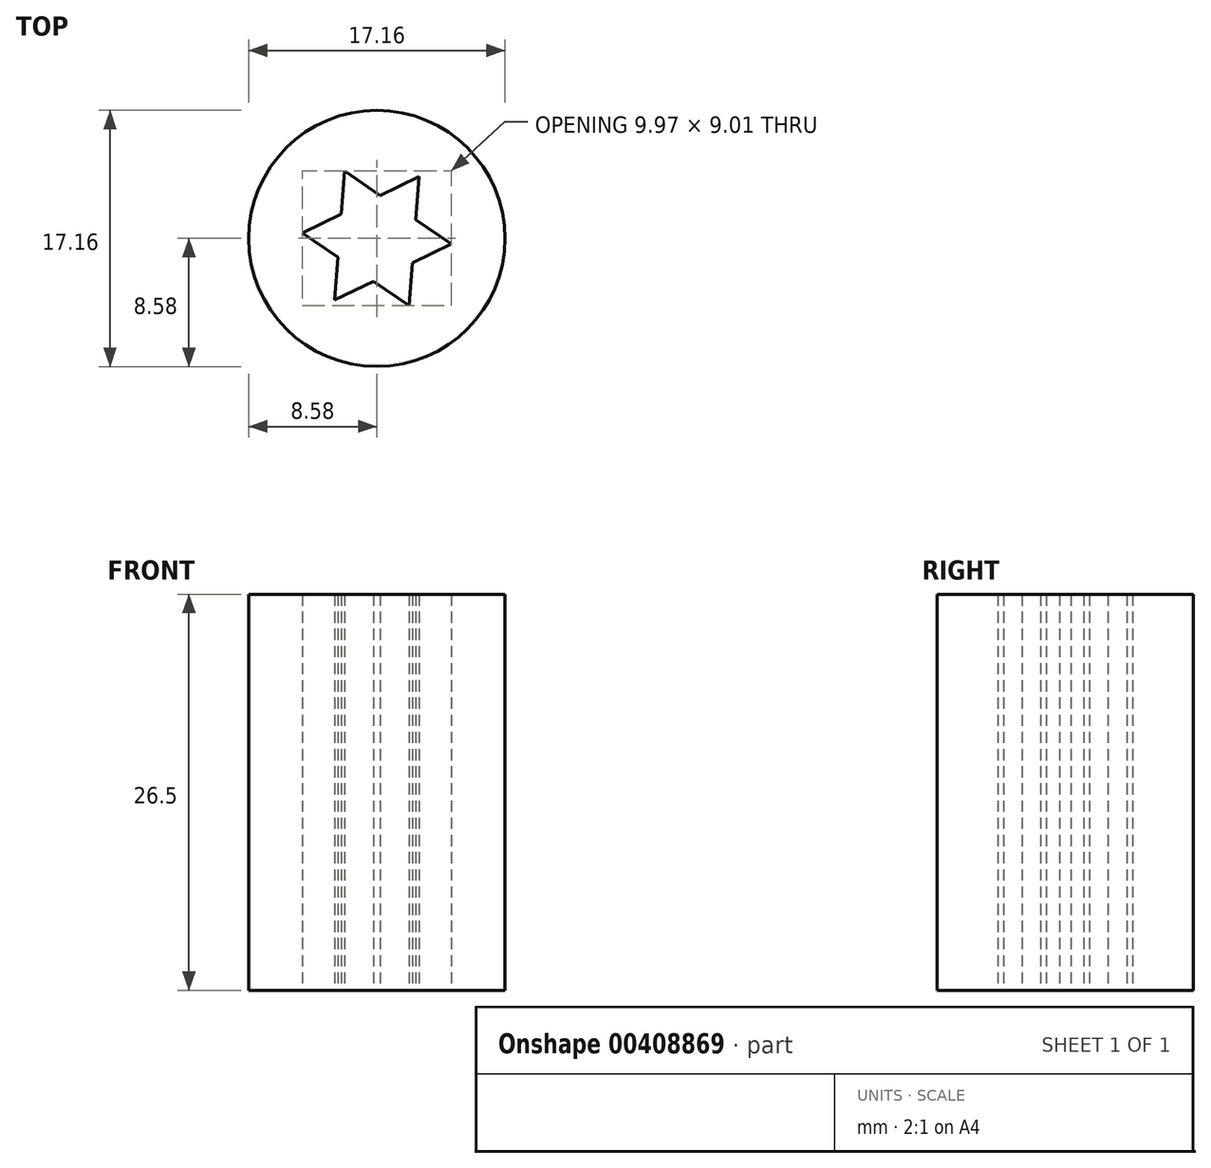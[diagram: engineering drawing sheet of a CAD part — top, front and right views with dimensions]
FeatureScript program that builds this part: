
annotation { "Feature Type Name" : "Feature", "Feature Type Description" : "" }
export const myFeature = defineFeature(function(context is Context, id is Id, definition is map)
    precondition{}
    {
        {
            var Q0;
            Q0=qCreatedBy(makeId("Top.planeOp"),FACE);
            var sketch = newSketch(context, id + "F0", { "sketchPlane" : qUnion([Q0])});
            skCircle(sketch, "E0", {"center": v(0, 0) * mm, "radius": 8.57 * mm});
            skSolve(sketch);
        }
        {
            var Q0;
            Q0 = qSketchRegion(id + "F0", true);
            extrude(context, id + "F1", {"entities" : qUnion([Q0]), "depth" : 26.5 * mm});
        }
        {
            var Q0;
            Q0=makeQuery(id+"F1.opExtrude","CAP_FACE",FACE,{"disambiguationData":[OSD([sQuery(id+"F0.wireOp",EDGE,"E0")])],"isStart":true});
            var sketch = newSketch(context, id + "F2", { "sketchPlane" : qUnion([Q0])});
            skCircle(sketch, "E1.cCircle", {"center": v(0, 0) * mm, "radius": 2.5 * mm, "construction": true});
            skLineSegment(sketch, "E1.0", {"start": v(-2.82, 4.13) * mm, "end": v(4.99, 0.38) * mm});
            skLineSegment(sketch, "E1.1", {"start": v(4.99, 0.38) * mm, "end": v(-2.17, -4.5) * mm});
            skLineSegment(sketch, "E1.2", {"start": v(-2.17, -4.5) * mm, "end": v(-2.82, 4.13) * mm});
            skPoint(sketch, "E1.0.midPoint", {"position": v(1.08, 2.25) * mm});
            skLineSegment(sketch, "E2.0", {"start": v(-4.99, -0.38) * mm, "end": v(2.17, 4.5) * mm});
            skLineSegment(sketch, "E2.1", {"start": v(2.17, 4.5) * mm, "end": v(2.82, -4.13) * mm});
            skLineSegment(sketch, "E2.2", {"start": v(2.82, -4.13) * mm, "end": v(-4.99, -0.38) * mm});
            skPoint(sketch, "E2.0.midPoint", {"position": v(-1.4, 2.06) * mm});
            skSolve(sketch);
        }
        {
            var Q0;
            {var subQ0=sQuery(id+"F2.wireOp",EDGE,"E1.1");var subQ1=sQuery(id+"F2.wireOp",EDGE,"E1.0");var subQ2=makeQuery(id+"F2.imprint","INTERSECT",VERTEX,{"derivedFrom":[subQ1,subQ0]});Q0=makeQuery(id+"F2.imprint","IMPRINT",FACE,{"disambiguationData":[TD([[makeQuery(id+"F2.imprint","IMPRINT",EDGE,{"disambiguationData":[TD([[subQ2,1.0]])],"derivedFrom":subQ1}),-1.0]])]});}
            var Q1;
            {var subQ0=sQuery(id+"F2.wireOp",EDGE,"E2.1");var subQ1=sQuery(id+"F2.wireOp",EDGE,"E1.1");var subQ2=makeQuery(id+"F2.imprint","INTERSECT",VERTEX,{"derivedFrom":[subQ1,subQ0]});Q1=makeQuery(id+"F2.imprint","IMPRINT",FACE,{"disambiguationData":[TD([[makeQuery(id+"F2.imprint","IMPRINT",EDGE,{"disambiguationData":[TD([[subQ2,-1.0]])],"derivedFrom":subQ1}),1.0]])]});}
            var Q2;
            {var subQ0=sQuery(id+"F2.wireOp",EDGE,"E1.2");var subQ1=sQuery(id+"F2.wireOp",EDGE,"E1.1");var subQ2=makeQuery(id+"F2.imprint","INTERSECT",VERTEX,{"derivedFrom":[subQ1,subQ0]});Q2=makeQuery(id+"F2.imprint","IMPRINT",FACE,{"disambiguationData":[TD([[makeQuery(id+"F2.imprint","IMPRINT",EDGE,{"disambiguationData":[TD([[subQ2,1.0]])],"derivedFrom":subQ1}),-1.0]])]});}
            var Q3;
            {var subQ0=sQuery(id+"F2.wireOp",EDGE,"E2.2");var subQ1=sQuery(id+"F2.wireOp",EDGE,"E1.2");var subQ2=makeQuery(id+"F2.imprint","INTERSECT",VERTEX,{"derivedFrom":[subQ1,subQ0]});Q3=makeQuery(id+"F2.imprint","IMPRINT",FACE,{"disambiguationData":[TD([[makeQuery(id+"F2.imprint","IMPRINT",EDGE,{"disambiguationData":[TD([[subQ2,-1.0]])],"derivedFrom":subQ1}),1.0]])]});}
            var Q4;
            {var subQ0=sQuery(id+"F2.wireOp",EDGE,"E2.0");var subQ1=sQuery(id+"F2.wireOp",EDGE,"E1.0");var subQ2=makeQuery(id+"F2.imprint","INTERSECT",VERTEX,{"derivedFrom":[subQ1,subQ0]});Q4=makeQuery(id+"F2.imprint","IMPRINT",FACE,{"disambiguationData":[TD([[makeQuery(id+"F2.imprint","IMPRINT",EDGE,{"disambiguationData":[TD([[subQ2,-1.0]])],"derivedFrom":subQ1}),-1.0]])]});}
            var Q5;
            {var subQ0=sQuery(id+"F2.wireOp",EDGE,"E2.0");var subQ1=sQuery(id+"F2.wireOp",EDGE,"E1.0");var subQ2=makeQuery(id+"F2.imprint","INTERSECT",VERTEX,{"derivedFrom":[subQ1,subQ0]});Q5=makeQuery(id+"F2.imprint","IMPRINT",FACE,{"disambiguationData":[TD([[makeQuery(id+"F2.imprint","IMPRINT",EDGE,{"disambiguationData":[TD([[subQ2,-1.0]])],"derivedFrom":subQ1}),1.0]])]});}
            var Q6;
            {var subQ0=sQuery(id+"F2.wireOp",EDGE,"E1.2");var subQ1=sQuery(id+"F2.wireOp",EDGE,"E1.0");var subQ2=makeQuery(id+"F2.imprint","INTERSECT",VERTEX,{"derivedFrom":[subQ1,subQ0]});Q6=makeQuery(id+"F2.imprint","IMPRINT",FACE,{"disambiguationData":[TD([[makeQuery(id+"F2.imprint","IMPRINT",EDGE,{"disambiguationData":[TD([[subQ2,-1.0]])],"derivedFrom":subQ1}),-1.0]])]});}
            extrude(context, id + "F3", {"entities" : qUnion([Q0, Q1, Q2, Q3, Q4, Q5, Q6]), "operationType" : NewBodyOperationType.REMOVE, "oppositeDirection" : true, "depth" : 26.5 * mm});
        }
    });
